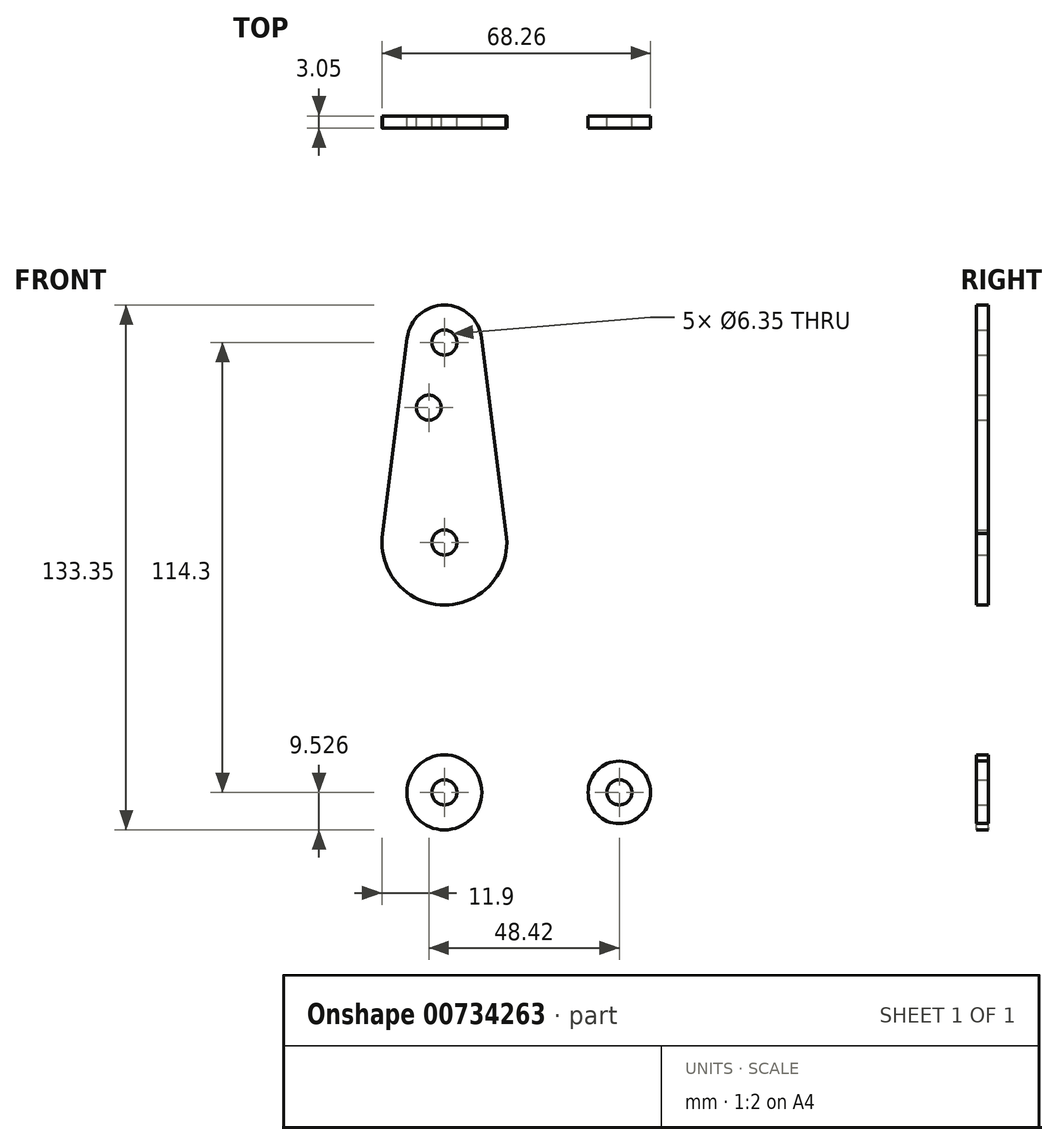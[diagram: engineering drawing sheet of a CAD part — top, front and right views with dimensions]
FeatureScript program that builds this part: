
annotation { "Feature Type Name" : "Feature", "Feature Type Description" : "" }
export const myFeature = defineFeature(function(context is Context, id is Id, definition is map)
    precondition{}
    {
        {
            var Q0;
            Q0=qCreatedBy(makeId("Front.planeOp"),FACE);
            var sketch = newSketch(context, id + "F0", { "sketchPlane" : qUnion([Q0])});
            skLineSegment(sketch, "E0", {"start": v(0, 102.67) * mm, "end": v(0, -11.63) * mm, "construction": true});
            skLineSegment(sketch, "E1", {"start": v(0, -11.63) * mm, "end": v(44.45, -11.63) * mm, "construction": true});
            skCircle(sketch, "E2", {"center": v(0, 102.67) * mm, "radius": 9.53 * mm});
            skCircle(sketch, "E3", {"center": v(0, 51.87) * mm, "radius": 15.88 * mm});
            skCircle(sketch, "E4", {"center": v(0, -11.63) * mm, "radius": 9.53 * mm});
            skCircle(sketch, "E5", {"center": v(44.45, -11.63) * mm, "radius": 7.94 * mm});
            skLineSegment(sketch, "E6", {"start": v(-15.79, 53.52) * mm, "end": v(-9.45, 103.86) * mm});
            skLineSegment(sketch, "E7", {"start": v(15.79, 53.52) * mm, "end": v(9.45, 103.86) * mm});
            skLineSegment(sketch, "E8", {"start": v(-9.48, -10.7) * mm, "end": v(-15.79, 50.21) * mm});
            skLineSegment(sketch, "E9", {"start": v(11.3, 5.96) * mm, "end": v(15.8, 50.27) * mm});
            skLineSegment(sketch, "E10", {"start": v(44.73, -3.7) * mm, "end": v(18.93, -2.78) * mm});
            skLineSegment(sketch, "E11", {"start": v(44.73, -19.57) * mm, "end": v(0, -21.16) * mm});
            skCircle(sketch, "E12", {"center": v(0, 102.67) * mm, "radius": 3.18 * mm});
            skCircle(sketch, "E13", {"center": v(-3.97, 86.11) * mm, "radius": 3.18 * mm});
            skCircle(sketch, "E14", {"center": v(0, 51.87) * mm, "radius": 3.18 * mm});
            skCircle(sketch, "E15", {"center": v(0, -11.63) * mm, "radius": 3.18 * mm});
            skCircle(sketch, "E16", {"center": v(44.45, -11.63) * mm, "radius": 3.18 * mm});
            skPoint(sketch, "E17.newPointB", {"position": v(0, -2.1) * mm});
            skArc(sketch, "E17.filletArc", {"start": v(11.3, 5.96) * mm, "mid": v(13.22, -0.06) * mm, "end": v(18.93, -2.78) * mm});
            skSolve(sketch);
        }
        {
            var Q0;
            Q0 = qSketchRegion(id + "F0", true);
            extrude(context, id + "F1", {"entities" : qUnion([Q0]), "depth" : 3.05 * mm, "offsetDistance" : 25.4 * mm});
        }
    });
